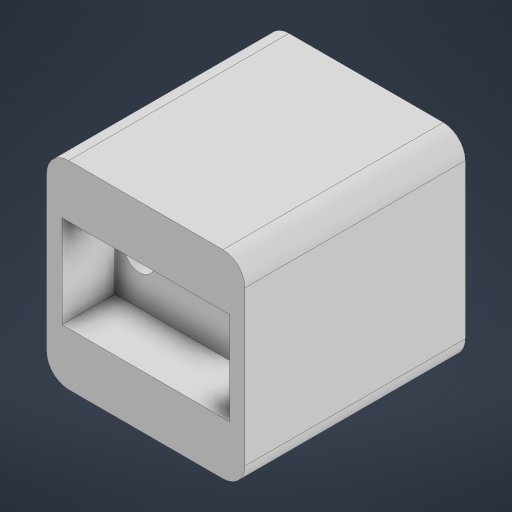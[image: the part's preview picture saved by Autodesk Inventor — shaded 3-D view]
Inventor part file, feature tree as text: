
AUTODESK INVENTOR PART (.ipt)
format: ipt  version: 2023 (Build 270158000, 158)  size: 200,192 bytes
history: native  units: mm
features: extrude x5, sketch x5, fillet x1
ambient origin geometry x8: Origin, YZ Plane, XZ Plane, XY Plane, X Axis, Y Axis, Z Axis, Center Point
bodies: Solid1 (feature_tree)
feature tree (11):
  extrude  "Extrusion1"  Depth=45.0mm
  fillet  "Fillet1"  Radius=50.0mm
  extrude  "Extrusion2"  Depth=5.0mm
  extrude  "Extrusion3"  Depth=20.0mm TaperAngle=0.0deg
  extrude  "Extrusion4"  Depth=12.0mm
  extrude  "Extrusion5"  Depth=21.0mm
  sketch  "Sketch1"  dims[d0=45.0mm d1=45.0mm d2=50.0mm d3=0.0mm]
  sketch  "Sketch2"  dims[d4=5.0mm d5=22.5mm]
  sketch  "Sketch3"  dims[d6=15.0mm d7=20.0mm d8=0.0mm]
  sketch  "Sketch4"  dims[d11=3.5mm d12=12.0mm]
  sketch  "Sketch5"  dims[d13=38.0mm d14=21.0mm d15=12.0mm d16=0.0mm d20=26.0mm d21=4.0mm d22=7.0mm d23=0.0mm d24=7.0mm d25=40.0mm d26=0.0mm d17=0.5mm d18=0.872665mm]
